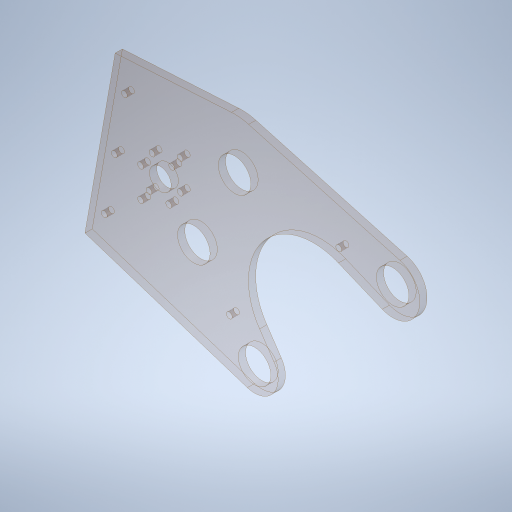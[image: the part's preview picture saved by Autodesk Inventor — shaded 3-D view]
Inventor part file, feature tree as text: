
AUTODESK INVENTOR PART (.ipt)
format: ipt  version: 2023.4 (Build 274418000, 418)  size: 354,816 bytes
history: native  units: in
note: dims shown in document units (in); Inventor stores cm internally (conversion verified against a paired STEP export)
features: sketch x1, extrude x1, hole x1
ambient origin geometry x8: Origin, YZ Plane, XZ Plane, XY Plane, X Axis, Y Axis, Z Axis, Center Point
bodies: Solid1 (feature_tree)
feature tree (3):
  sketch  "Sketch1"  dims[d3=45.0deg d4=0.0in d7=2.0in d8=4.25in d9=1.125in d10=3.0in d11=4.5in d12=4.5in d13=0.25in d14=0.375in d15=5.499in d16=1.128in d17=3.341in d18=3.126in d19=3.126in d22=1.0in d23=6.0in d26=8.0293in d27=2.0in d28=0.4688in d29=0.3504in d30=6.75in d31=0.0687in d32=0.75in d33=4.0in d34=1.375in d35=0.75in d36=0.25in d37=1.375in d38=2.3622in d40=360.0deg d43=0.1718in d44=0.375in d45=0.25in d46=0.0in d47=0.201in d48=0.75in d49=0.37in d50=0.25in d51=90.0deg d52=1.0in d53=0.8108in d55=0.5497in d56=0.3in]
  extrude  "Extrusion1"  TaperAngle=0.0deg  [1 undecoded]
  hole  "Hole1"  [1 undecoded]
note: 2 required parameter values undecoded (feature->parameter linkage not recoverable at this tier; creation-order binding heuristic only, values carry confidence <= 0.55)
